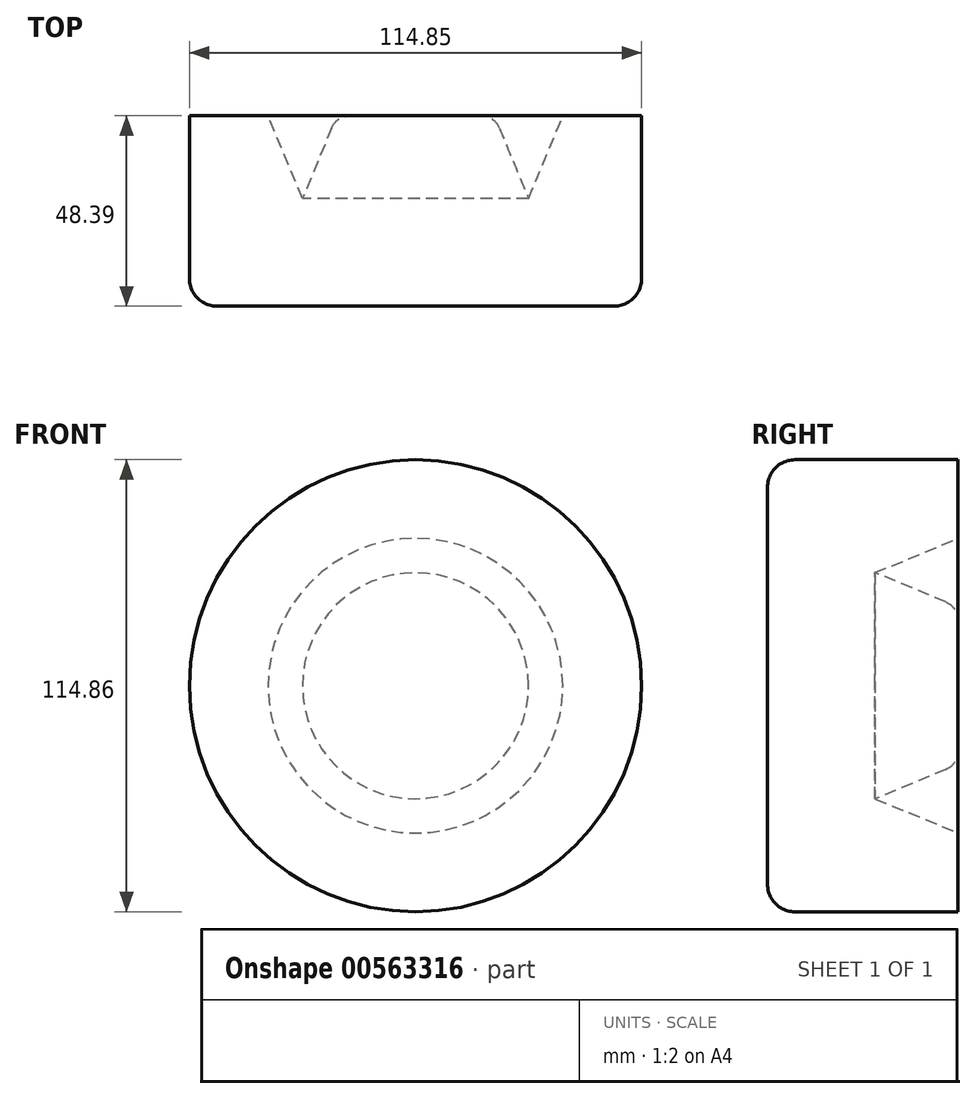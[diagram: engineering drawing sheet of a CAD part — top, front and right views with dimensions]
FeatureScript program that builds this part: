
annotation { "Feature Type Name" : "Feature", "Feature Type Description" : "" }
export const myFeature = defineFeature(function(context is Context, id is Id, definition is map)
    precondition{}
    {
        {
            var Q0;
            Q0=qCreatedBy(makeId("Top.planeOp"),FACE);
            var sketch = newSketch(context, id + "F0", { "sketchPlane" : qUnion([Q0])});
            skLineSegment(sketch, "E0.bottom", {"start": v(-21.71, -19.85) * mm, "end": v(28.71, -19.85) * mm});
            skLineSegment(sketch, "E0.top", {"start": v(-28.71, 28.54) * mm, "end": v(-8.71, 28.54) * mm});
            skLineSegment(sketch, "E0.left", {"start": v(-28.71, -12.85) * mm, "end": v(-28.71, 28.54) * mm});
            skLineSegment(sketch, "E0.right", {"start": v(28.71, -19.85) * mm, "end": v(28.71, 28.54) * mm});
            skPoint(sketch, "E1.visualSharp", {"position": v(-28.71, -19.85) * mm});
            skArc(sketch, "E1.filletArc", {"start": v(-28.71, -12.85) * mm, "mid": v(-26.66, -17.8) * mm, "end": v(-21.71, -19.85) * mm});
            skPoint(sketch, "E2", {"position": v(-8.71, 28.54) * mm});
            skPoint(sketch, "E3", {"position": v(8.71, 28.54) * mm});
            skLineSegment(sketch, "E4", {"start": v(-8.71, 28.54) * mm, "end": v(0, 7.5) * mm});
            skLineSegment(sketch, "E5", {"start": v(8.71, 28.54) * mm, "end": v(-0.32, 6.74) * mm});
            skLineSegment(sketch, "E6.trimOffspring", {"start": v(8.71, 28.54) * mm, "end": v(28.71, 28.54) * mm});
            skSolve(sketch);
        }
        {
            var Q0;
            Q0=makeQuery(id+"F0.imprint","IMPRINT",FACE,{"disambiguationData":[TD([[makeQuery(id+"F0.imprint","IMPRINT",EDGE,{"derivedFrom":sQuery(id+"F0.wireOp",EDGE,"E0.bottom")}),1.0]])]});
            var Q1;
            Q1=sQuery(id+"F0.wireOp",EDGE,"E0.right");
            revolve(context, id + "F1", {"entities" : qUnion([Q0]), "axis" : qUnion([Q1]), "revolveType" : RevolveType.FULL});
        }
        {
            var Q0;
            Q0=makeQuery(id+"F1.opRevolve","SWEPT_EDGE",EDGE,{"disambiguationData":[OSD([sQuery(id+"F0.wireOp",EDGE,"E5"),sQuery(id+"F0.wireOp",EDGE,"E6.trimOffspring")])]});
            fillet(context, id + "F2", {"entities" : qUnion([Q0]), "radius" : 5 * mm, "tangentPropagation" : true, "allowEdgeOverflow" : false});
        }
    });
